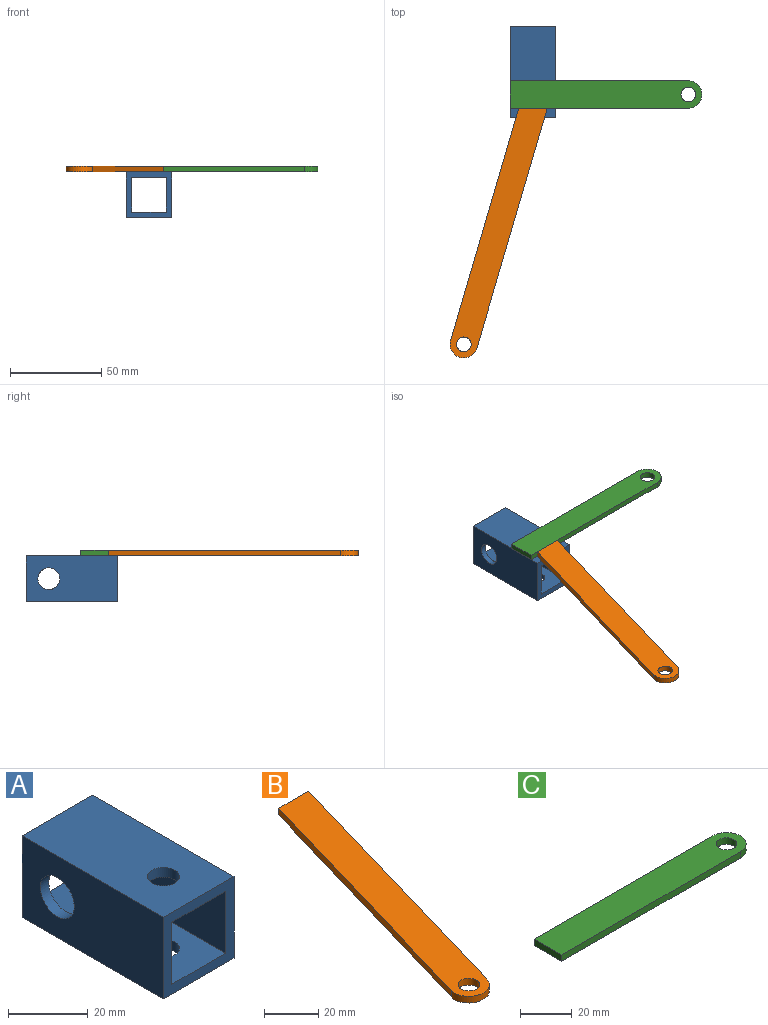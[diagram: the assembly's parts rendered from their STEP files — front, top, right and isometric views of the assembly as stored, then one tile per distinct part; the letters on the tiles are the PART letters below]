
ASSEMBLY  parts=3 mates=2
PART A: 14 faces, bbox 25x50x25 mm
  f0: cylinder r=6mm len=12mm, axis (-1,0,0), area 113.1mm2, adj f3,f9
  f1: plane 50x25mm, normal (-1,0,0), area 1136.9mm2, adj f2,f4,f5,f6,f7
  f2: plane 25x25mm, normal (0,-1,0), area 264mm2, adj f1,f3,f5,f6,f8,f9,f10,f11
  f3: plane 50x25mm, normal (1,0,0), area 1136.9mm2, adj f0,f2,f4,f5,f6
  f4: plane 25x25mm, normal (0,1,0), area 264mm2, adj f1,f3,f5,f6,f8,f9,f10,f11
  f5: plane 50x25mm, normal (0,0,-1), area 1199.7mm2, adj f1,f2,f3,f4,f13
  f6: plane 50x25mm, normal (0,0,1), area 1199.7mm2, adj f1,f2,f3,f4,f12
  f7: cylinder r=6mm len=12mm, axis (-1,0,0), area 113.1mm2, adj f1,f8
  f8: plane 50x19mm, normal (1,0,0), area 836.9mm2, adj f2,f4,f7,f10,f11
  f9: plane 50x19mm, normal (-1,0,0), area 836.9mm2, adj f0,f2,f4,f10,f11
  f10: plane 50x19mm, normal (0,0,1), area 899.7mm2, adj f2,f4,f8,f9,f13
  f11: plane 50x19mm, normal (0,0,-1), area 899.7mm2, adj f2,f4,f8,f9,f12
  f12: cylinder r=4mm len=8mm, axis (0,0,1), area 75.4mm2, adj f6,f11
  f13: cylinder r=4mm len=8mm, axis (0,0,1), area 75.4mm2, adj f5,f10
PART B: 7 faces, bbox 53.2x136.7x3 mm
  f0: plane 127.14x37.27mm, normal (-0.96,0.28,0), area 397.5mm2, adj f1,f4,f5,f6
  f1: cylinder r=7.5mm len=14.7mm, axis (0,0,-1), area 70.7mm2, adj f0,f2,f5,f6
  f2: plane 131.36x38.5mm, normal (0.96,-0.28,0), area 410.6mm2, adj f1,f4,f5,f6
  f3: cylinder r=4mm len=8mm, axis (0,0,-1), area 75.4mm2, adj f5,f6
  f4: plane 15.63x3mm, normal (0,1,0), area 46.9mm2, adj f0,f2,f5,f6
  f5: plane 136.75x53.2mm, normal (0,0,1), area 2058.4mm2, adj f0,f1,f2,f3,f4
  f6: plane 136.75x53.2mm, normal (0,0,-1), area 2058.4mm2, adj f0,f1,f2,f3,f4
PART C: 7 faces, bbox 105x15x3 mm
  f0: plane 97.5x3mm, normal (0,-1,0), area 292.5mm2, adj f1,f4,f5,f6
  f1: cylinder r=7.5mm len=15mm, axis (0,0,-1), area 70.7mm2, adj f0,f2,f5,f6
  f2: plane 97.5x3mm, normal (0,1,0), area 292.5mm2, adj f1,f4,f5,f6
  f3: cylinder r=4mm len=8mm, axis (0,0,-1), area 75.4mm2, adj f5,f6
  f4: plane 15x3mm, normal (-1,0,0), area 45mm2, adj f0,f2,f5,f6
  f5: plane 105x15mm, normal (0,0,1), area 1500.6mm2, adj f0,f1,f2,f3,f4
  f6: plane 105x15mm, normal (0,0,-1), area 1500.6mm2, adj f0,f1,f2,f3,f4
PLACE A rot(axis=(0,1,0),180deg) t=(36.91,67.61,-18.34)mm
PLACE B t=(39.11,67.61,-18.34)mm
PLACE C rot(axis=(1,0,0),180deg) t=(36.91,67.61,-15.34)mm
MATE fastened C.f5 <-> A.f5  axis (0,0,-1) through (24.41,67.61,-18.34)mm
MATE fastened B.f6 <-> A.f5  axis (0,0,-1) through (36.91,60.11,-18.34)mm
